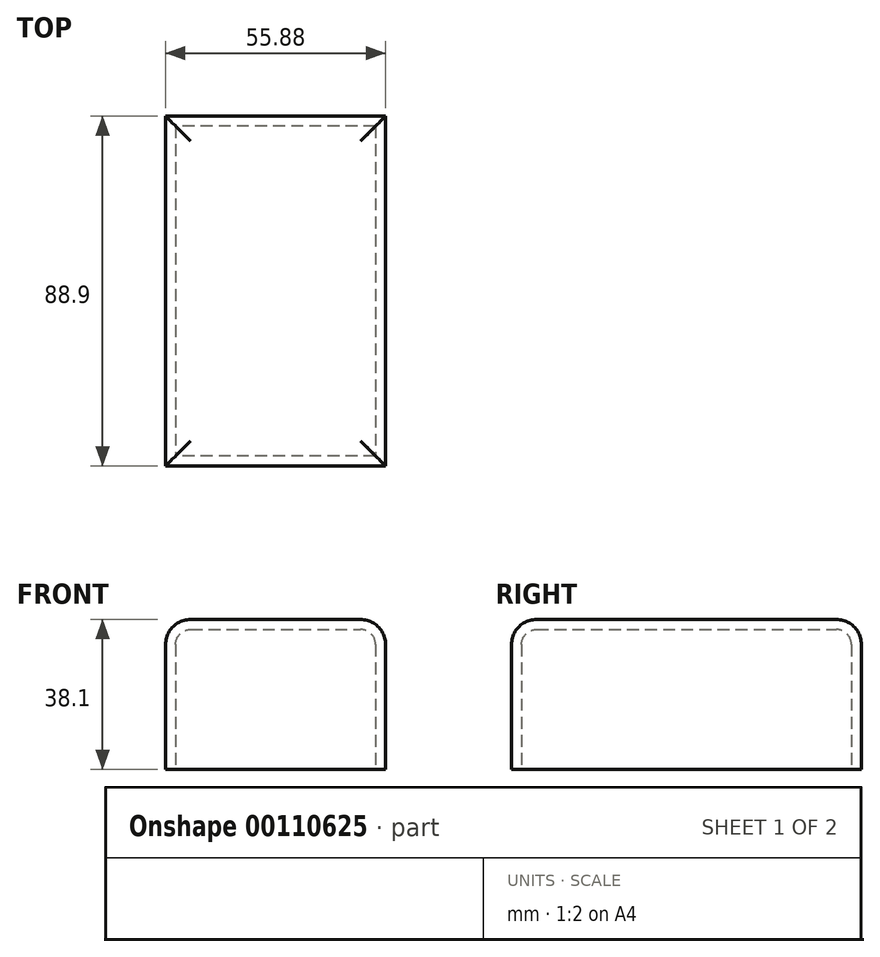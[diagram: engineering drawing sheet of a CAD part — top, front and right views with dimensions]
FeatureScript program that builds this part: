
annotation { "Feature Type Name" : "Feature", "Feature Type Description" : "" }
export const myFeature = defineFeature(function(context is Context, id is Id, definition is map)
    precondition{}
    {
        {
            var Q0;
            Q0=qCreatedBy(makeId("Top.planeOp"),FACE);
            var sketch = newSketch(context, id + "F0", { "sketchPlane" : qUnion([Q0])});
            skLineSegment(sketch, "E0.rect.bottom", {"start": v(27.94, 44.45) * mm, "end": v(-27.94, 44.45) * mm});
            skLineSegment(sketch, "E0.rect.top", {"start": v(27.94, -44.45) * mm, "end": v(-27.94, -44.45) * mm});
            skLineSegment(sketch, "E0.rect.left", {"start": v(27.94, 44.45) * mm, "end": v(27.94, -44.45) * mm});
            skLineSegment(sketch, "E0.rect.right", {"start": v(-27.94, 44.45) * mm, "end": v(-27.94, -44.45) * mm});
            skPoint(sketch, "E0.rect.middle", {"position": v(0, 0) * mm});
            skSolve(sketch);
        }
        {
            var Q0;
            Q0=qSketchRegion(id+"F0",true);
            extrude(context, id + "F1", {"entities" : qUnion([Q0]), "depth" : 38.1 * mm});
        }
        {
            var Q0;
            Q0=makeQuery(id+"F1.opExtrude","CAP_EDGE",EDGE,{"disambiguationData":[OSD([sQuery(id+"F0.wireOp",EDGE,"E0.rect.top")])],"isStart":false});
            var Q1;
            Q1=makeQuery(id+"F1.opExtrude","CAP_EDGE",EDGE,{"disambiguationData":[OSD([sQuery(id+"F0.wireOp",EDGE,"E0.rect.right")])],"isStart":false});
            var Q2;
            Q2=makeQuery(id+"F1.opExtrude","CAP_EDGE",EDGE,{"disambiguationData":[OSD([sQuery(id+"F0.wireOp",EDGE,"E0.rect.left")])],"isStart":false});
            var Q3;
            Q3=makeQuery(id+"F1.opExtrude","CAP_EDGE",EDGE,{"disambiguationData":[OSD([sQuery(id+"F0.wireOp",EDGE,"E0.rect.bottom")])],"isStart":false});
            fillet(context, id + "F2", {"entities" : qUnion([Q0, Q1, Q2, Q3]), "radius" : 6.35 * mm, "tangentPropagation" : true, "allowEdgeOverflow" : false});
        }
        {
            var Q0;
            Q0=makeQuery(id+"F1.opExtrude","CAP_FACE",FACE,{"disambiguationData":[OSD([sQuery(id+"F0.wireOp",EDGE,"E0.rect.bottom"),sQuery(id+"F0.wireOp",EDGE,"E0.rect.top"),sQuery(id+"F0.wireOp",EDGE,"E0.rect.left"),sQuery(id+"F0.wireOp",EDGE,"E0.rect.right")])],"isStart":true});
            shell(context, id + "F3", {"entities" : qUnion([Q0]), "thickness" : 2.54 * mm});
        }
    });
